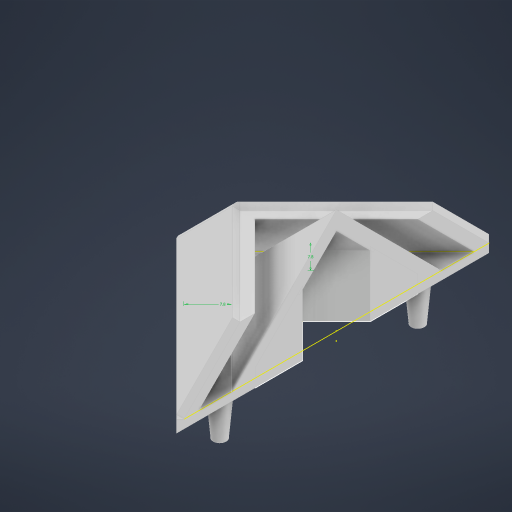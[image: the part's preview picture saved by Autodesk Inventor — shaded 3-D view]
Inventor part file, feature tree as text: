
AUTODESK INVENTOR PART (.ipt)
format: ipt  version: 2023 (Build 270158000, 158)  size: 448,000 bytes
history: native  units: mm
features: extrude x20, sketch x20, plane x6, split x2, shell x2, draft x1, revolve x1
ambient origin geometry x8: Origin, YZ Plane, XZ Plane, XY Plane, X Axis, Y Axis, Z Axis, Center Point
bodies: Solid1 (feature_tree), Solid4 (feature_tree)
feature tree (52):
  extrude  "Extrusion1"  Depth=2.0mm TaperAngle=0.0deg
  sketch  "Sketch3"  dims[d1=50.0mm d2=2.0mm d3=0.0mm]
  sketch  "Sketch12"  dims[d41=70.71mm d42=50.0mm d43=50.0mm]
  plane  "Work Plane5"
  plane  "Work Plane6"
  extrude  "Extrusion10"  Depth=50.0mm
  split  "Split3"
  shell  "Shell3"  Thickness=50.0mm
  sketch  "Sketch13"  dims[d44=10.0mm d45=0.0mm d46=0.0mm d47=7.8mm]
  plane  "Work Plane9"
  plane  "Work Plane10"
  extrude  "Extrusion18"  TaperAngle=0.0deg  [1 undecoded]
  split  "Split5"
  shell  "Shell5"  Thickness=7.8mm
  extrude  "Extrusion24"  Depth=2.0mm
  extrude  "Extrusion25"  Depth=7.8mm
  extrude  "Extrusion26"  Depth=2.0mm
  extrude  "Extrusion27"  Depth=2.0mm TaperAngle=0.0deg
  draft  "FaceDraft3"
  plane  "Work Plane12"
  extrude  "Extrusion28"  Depth=10.0mm
  sketch  "Sketch31"  dims[d117=3.0mm d118=3.0mm]
  extrude  "Extrusion29"  Depth=3.0mm
  extrude  "Extrusion30"  Depth=10.0mm
  sketch  "Sketch33"  dims[d119=10.0mm d120=0.0mm d121=0.872665mm]
  sketch  "Sketch34"  dims[d122=-15.0mm d123=30.0mm d124=0.0mm]
  extrude  "Extrusion31"  Depth=30.0mm TaperAngle=0.0deg
  extrude  "Extrusion32"  Depth=10.0mm TaperAngle=0.0deg
  extrude  "Extrusion33"  Depth=10.0mm
  extrude  "Extrusion34"  Depth=2.45mm TaperAngle=0.0deg
  extrude  "Extrusion35"  Depth=2.45mm TaperAngle=0.0deg
  extrude  "Extrusion36"  Depth=2.45mm TaperAngle=0.0deg
  extrude  "Extrusion37"  Depth=1.5mm TaperAngle=0.0deg
  extrude  "Extrusion38"  Depth=1.5mm TaperAngle=0.0deg
  extrude  "Extrusion39"  Depth=0.872665mm
  extrude  "Extrusion40"  [1 undecoded]
  revolve  "Revolution1"  [1 undecoded]
  sketch  "Sketch25"  dims[d48=7.8mm d49=2.0mm]
  sketch  "Sketch27"  dims[d52=7.8mm d53=7.8mm]
  sketch  "Sketch28"  dims[d85=10.0mm d86=0.0mm d87=2.0mm]
  sketch  "Sketch29"  dims[d110=2.0mm d111=0.0mm d112=2.0mm d113=0.0mm]
  plane  "Work Plane11"
  sketch  "Sketch30"  dims[d114=10.0mm d115=0.0mm d116=3.0mm]
  sketch  "Sketch35"  dims[d125=10.0mm d126=0.0mm d127=10.0mm d128=0.0mm]
  sketch  "Sketch37"  dims[d129=10.0mm d130=10.0mm]
  sketch  "Sketch38"  dims[d131=2.45mm d132=0.0mm d133=2.45mm d134=0.0mm]
  sketch  "Sketch39"  dims[d135=2.45mm d136=0.0mm d138=2.45mm d139=0.0mm]
  sketch  "Sketch40"  dims[d140=2.45mm d141=0.0mm d142=2.45mm d143=0.0mm]
  sketch  "Sketch41"  dims[d144=1.5mm d145=0.0mm d146=1.5mm d147=0.0mm]
  sketch  "Sketch42"  dims[d148=1.5mm d149=0.0mm d150=1.5mm d151=0.0mm]
  sketch  "Sketch43"  dims[d152=75.0deg d88=0.872665mm]
  sketch  "Sketch44"  dims[d137=0.5mm]
note: 3 required parameter values undecoded (feature->parameter linkage not recoverable at this tier; creation-order binding heuristic only, values carry confidence <= 0.55)
